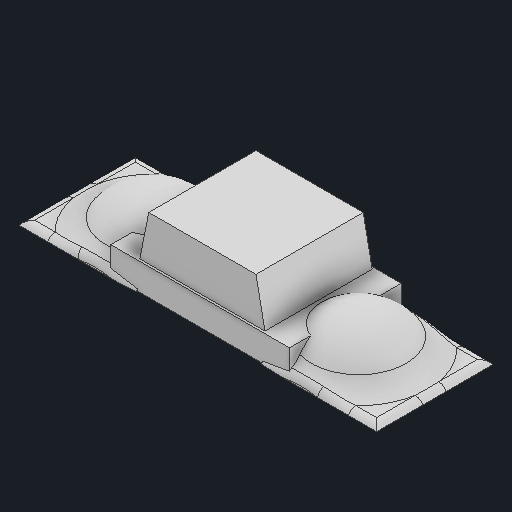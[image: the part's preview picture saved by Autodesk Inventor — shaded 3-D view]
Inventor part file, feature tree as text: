
AUTODESK INVENTOR PART (.ipt)
format: ipt  version: 2023 (Build 270158000, 158)  size: 199,680 bytes
history: native  units: in
note: dims shown in document units (in); Inventor stores cm internally (conversion verified against a paired STEP export)
features: mirror x1, other x1
ambient origin geometry x8: Origin, YZ Plane, XZ Plane, XY Plane, X Axis, Y Axis, Z Axis, Center Point
bodies: Solid1 (feature_tree), Solid2 (feature_tree)
feature tree (2):
  mirror  "Mirror3"
  other  "Boss-Extrude5"
